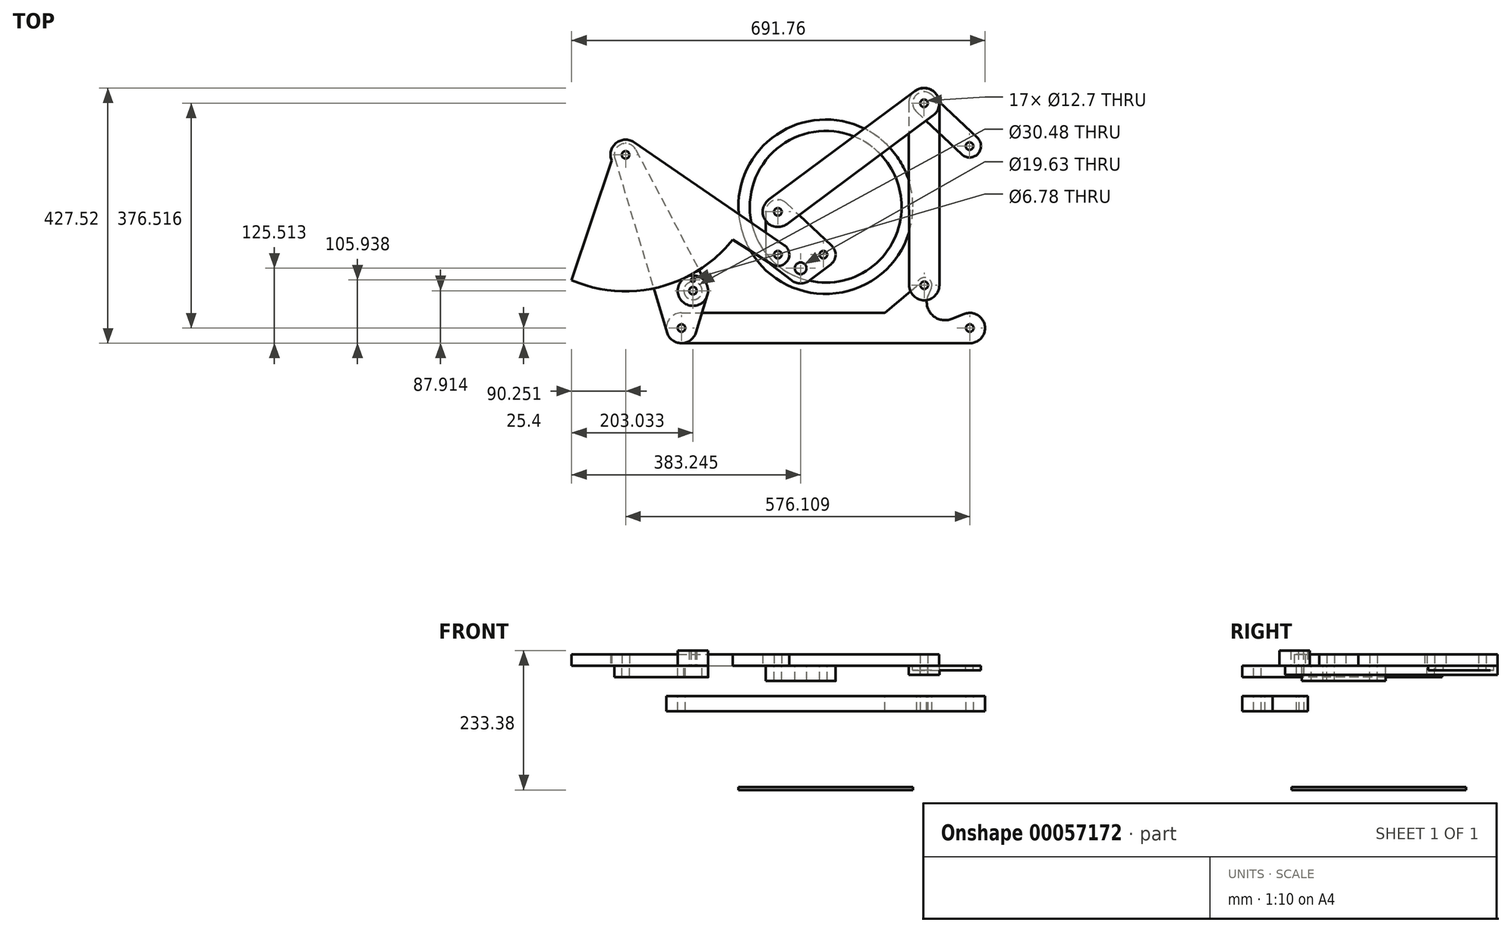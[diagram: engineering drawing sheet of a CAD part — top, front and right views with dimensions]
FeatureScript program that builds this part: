
annotation { "Feature Type Name" : "Feature", "Feature Type Description" : "" }
export const myFeature = defineFeature(function(context is Context, id is Id, definition is map)
    precondition{}
    {
        {
            var Q0;
            Q0=qCreatedBy(makeId("Top.planeOp"),FACE);
            var sketch = newSketch(context, id + "F0", { "sketchPlane" : qUnion([Q0])});
            skLineSegment(sketch, "E0.rect.bottom", {"start": v(-381, 228.6) * mm, "end": v(381, 228.6) * mm});
            skLineSegment(sketch, "E0.rect.top", {"start": v(-381, -228.6) * mm, "end": v(381, -228.6) * mm});
            skLineSegment(sketch, "E0.rect.left", {"start": v(-381, 228.6) * mm, "end": v(-381, -228.6) * mm});
            skLineSegment(sketch, "E0.rect.right", {"start": v(381, 228.6) * mm, "end": v(381, -228.6) * mm});
            skPoint(sketch, "E0.rect.middle", {"position": v(0, 0) * mm});
            skLineSegment(sketch, "E1", {"start": v(-241.3, -203.2) * mm, "end": v(241.3, -203.2) * mm, "construction": true});
            skLineSegment(sketch, "E2", {"start": v(0, -203.2) * mm, "end": v(0, 0) * mm, "construction": true});
            skLineSegment(sketch, "E3", {"start": v(-241.3, -203.2) * mm, "end": v(-334.8, 86.9) * mm});
            skLineSegment(sketch, "E4", {"start": v(-334.8, 86.9) * mm, "end": v(-79.92, -80.23) * mm});
            skLineSegment(sketch, "E5", {"start": v(-3.72, -80.23) * mm, "end": v(240.91, 101.6) * mm});
            skLineSegment(sketch, "E6", {"start": v(240.91, 101.6) * mm, "end": v(241.3, -203.2) * mm});
            skCircle(sketch, "E7", {"center": v(0, 0) * mm, "radius": 139.7 * mm});
            skArc(sketch, "E8", {"start": v(57.44, -34.77) * mm, "mid": v(188.02, -120.8) * mm, "end": v(343.35, -102.76) * mm});
            skArc(sketch, "E9", {"start": v(-425.06, -123.13) * mm, "mid": v(-268.94, -132) * mm, "end": v(-143.64, -38.45) * mm});
            skLineSegment(sketch, "E10", {"start": v(-425.06, -123.13) * mm, "end": v(-334.8, 86.9) * mm});
            skLineSegment(sketch, "E11", {"start": v(240.91, 101.6) * mm, "end": v(343.35, -102.76) * mm});
            skCircle(sketch, "E12", {"center": v(195.05, -148.23) * mm, "radius": 25.4 * mm});
            skLineSegment(sketch, "E13", {"start": v(195.05, -148.23) * mm, "end": v(241.3, -203.2) * mm});
            skCircle(sketch, "E14", {"center": v(-222.03, -140.69) * mm, "radius": 25.4 * mm});
            skLineSegment(sketch, "E15", {"start": v(-222.03, -140.69) * mm, "end": v(-241.3, -203.2) * mm});
            skLineSegment(sketch, "E16", {"start": v(-381, 76.2) * mm, "end": v(-228.6, 228.6) * mm});
            skLineSegment(sketch, "E17", {"start": v(381, 76.2) * mm, "end": v(228.6, 228.6) * mm});
            skLineSegment(sketch, "E18", {"start": v(195.05, -148.23) * mm, "end": v(240.91, 101.6) * mm, "construction": true});
            skLineSegment(sketch, "E19", {"start": v(-222.03, -140.69) * mm, "end": v(-334.8, 86.9) * mm, "construction": true});
            skLineSegment(sketch, "E20", {"start": v(-3.72, -80.23) * mm, "end": v(-79.92, -80.23) * mm});
            skLineSegment(sketch, "E21", {"start": v(-79.92, -80.23) * mm, "end": v(-79.92, -8.51) * mm});
            skLineSegment(sketch, "E22", {"start": v(-79.92, -8.51) * mm, "end": v(164.71, 173.32) * mm});
            skLineSegment(sketch, "E23", {"start": v(164.71, 173.32) * mm, "end": v(165.1, -131.48) * mm});
            skLineSegment(sketch, "E24", {"start": v(-79.92, -8.51) * mm, "end": v(-3.72, -80.23) * mm});
            skLineSegment(sketch, "E25", {"start": v(164.71, 173.32) * mm, "end": v(240.91, 101.6) * mm});
            skLineSegment(sketch, "E26", {"start": v(-41.82, -80.23) * mm, "end": v(-41.82, -103.09) * mm});
            skLineSegment(sketch, "E27", {"start": v(165.1, -131.48) * mm, "end": v(241.3, -203.2) * mm});
            skSolve(sketch);
        }
        {
            var Q0;
            Q0=qCreatedBy(makeId("Top.planeOp"),FACE);
            var sketch = newSketch(context, id + "F1", { "sketchPlane" : qUnion([Q0])});
            skCircle(sketch, "E28", {"center": v(-334.8, 86.9) * mm, "radius": 25.4 * mm});
            skCircle(sketch, "E29", {"center": v(-79.92, -80.23) * mm, "radius": 19.05 * mm});
            skArc(sketch, "E30", {"start": v(-425.06, -123.13) * mm, "mid": v(-259.1, -128.8) * mm, "end": v(-133.1, -20.65) * mm});
            skLineSegment(sketch, "E31", {"start": v(-320.44, 107.85) * mm, "end": v(-69.14, -64.52) * mm});
            skLineSegment(sketch, "E32", {"start": v(-348.3, 65.38) * mm, "end": v(-90.03, -96.37) * mm});
            skLineSegment(sketch, "E33", {"start": v(-425.06, -123.13) * mm, "end": v(-358.3, 77.22) * mm});
            skCircle(sketch, "E34", {"center": v(-334.8, 86.9) * mm, "radius": 6.35 * mm});
            skCircle(sketch, "E35", {"center": v(-79.92, -80.23) * mm, "radius": 6.35 * mm});
            skSolve(sketch);
        }
        {
            var Q0;
            Q0=makeQuery(id+"F1.imprint","IMPRINT",FACE,{"disambiguationData":[TD([[makeQuery(id+"F1.imprint","IMPRINT",EDGE,{"derivedFrom":sQuery(id+"F1.wireOp",EDGE,"E34")}),-1.0]])]});
            var Q1;
            {var subQ3=sQuery(id+"F1.wireOp",EDGE,"E28");var subQ5=sQuery(id+"F1.wireOp",EDGE,"E31");var subQ6=makeQuery(id+"F1.imprint","INTERSECT",VERTEX,{"derivedFrom":[subQ3,subQ5]});Q1=makeQuery(id+"F1.imprint","IMPRINT",FACE,{"disambiguationData":[TD([[makeQuery(id+"F1.imprint","IMPRINT",EDGE,{"disambiguationData":[TD([[subQ6,1.0]])],"derivedFrom":subQ3}),-1.0]])]});}
            var Q2;
            {var subQ3=sQuery(id+"F1.wireOp",EDGE,"E29");var subQ5=sQuery(id+"F1.wireOp",EDGE,"E31");var subQ6=makeQuery(id+"F1.imprint","INTERSECT",VERTEX,{"derivedFrom":[subQ3,subQ5]});Q2=makeQuery(id+"F1.imprint","IMPRINT",FACE,{"disambiguationData":[TD([[makeQuery(id+"F1.imprint","IMPRINT",EDGE,{"disambiguationData":[TD([[subQ6,-1.0]])],"derivedFrom":subQ3}),-1.0]])]});}
            var Q3;
            Q3=makeQuery(id+"F1.imprint","IMPRINT",FACE,{"disambiguationData":[TD([[makeQuery(id+"F1.imprint","IMPRINT",EDGE,{"derivedFrom":sQuery(id+"F1.wireOp",EDGE,"E35")}),-1.0]])]});
            var Q4;
            {var subQ0=sQuery(id+"F1.wireOp",EDGE,"E33");Q4=makeQuery(id+"F1.imprint","IMPRINT",FACE,{"disambiguationData":[TD([[makeQuery(id+"F1.imprint","IMPRINT",EDGE,{"derivedFrom":subQ0}),-1.0]])]});}
            extrude(context, id + "F2", {"entities" : qUnion([Q0, Q1, Q2, Q3, Q4]), "depth" : 19.05 * mm});
        }
        {
            var Q0;
            Q0=qCreatedBy(makeId("Top.planeOp"),FACE);
            var sketch = newSketch(context, id + "F3", { "sketchPlane" : qUnion([Q0])});
            skCircle(sketch, "E36", {"center": v(-334.8, 86.9) * mm, "radius": 19.05 * mm});
            skCircle(sketch, "E37", {"center": v(-222.03, -140.69) * mm, "radius": 25.4 * mm});
            skCircle(sketch, "E38", {"center": v(-241.3, -203.2) * mm, "radius": 25.4 * mm});
            skLineSegment(sketch, "E39", {"start": v(-353.06, 81.44) * mm, "end": v(-265.63, -210.49) * mm});
            skLineSegment(sketch, "E40", {"start": v(-317.96, 95.78) * mm, "end": v(-199.56, -128.84) * mm});
            skLineSegment(sketch, "E41", {"start": v(-217.03, -210.68) * mm, "end": v(-197.75, -148.17) * mm});
            skCircle(sketch, "E42", {"center": v(-334.8, 86.9) * mm, "radius": 6.35 * mm});
            skCircle(sketch, "E43", {"center": v(-222.03, -140.69) * mm, "radius": 15.24 * mm});
            skCircle(sketch, "E44", {"center": v(-241.3, -203.2) * mm, "radius": 6.35 * mm});
            skSolve(sketch);
        }
        {
            var Q0;
            Q0=makeQuery(id+"F3.imprint","IMPRINT",FACE,{"disambiguationData":[TD([[makeQuery(id+"F3.imprint","IMPRINT",EDGE,{"derivedFrom":sQuery(id+"F3.wireOp",EDGE,"E42")}),-1.0]])]});
            var Q1;
            {var subQ2=sQuery(id+"F3.wireOp",EDGE,"E39");Q1=makeQuery(id+"F3.imprint","IMPRINT",FACE,{"disambiguationData":[TD([[makeQuery(id+"F3.imprint","IMPRINT",EDGE,{"derivedFrom":subQ2}),1.0]])]});}
            var Q2;
            Q2=makeQuery(id+"F3.imprint","IMPRINT",FACE,{"disambiguationData":[TD([[makeQuery(id+"F3.imprint","IMPRINT",EDGE,{"derivedFrom":sQuery(id+"F3.wireOp",EDGE,"E43")}),-1.0]])]});
            var Q3;
            Q3=makeQuery(id+"F3.imprint","IMPRINT",FACE,{"disambiguationData":[TD([[makeQuery(id+"F3.imprint","IMPRINT",EDGE,{"derivedFrom":sQuery(id+"F3.wireOp",EDGE,"E44")}),-1.0]])]});
            extrude(context, id + "F4", {"entities" : qUnion([Q0, Q1, Q2, Q3]), "oppositeDirection" : true, "depth" : 19.05 * mm});
        }
        {
            var Q0;
            Q0=qCreatedBy(makeId("Top.planeOp"),FACE);
            var sketch = newSketch(context, id + "F5", { "sketchPlane" : qUnion([Q0])});
            skCircle(sketch, "E45", {"center": v(-222.03, -140.69) * mm, "radius": 25.4 * mm});
            skCircle(sketch, "E46", {"center": v(-222.03, -140.69) * mm, "radius": 6.35 * mm});
            skCircle(sketch, "E47", {"center": v(-222.03, -122.66) * mm, "radius": 3.4 * mm});
            skSolve(sketch);
        }
        {
            var Q0;
            Q0=makeQuery(id+"F5.imprint","IMPRINT",FACE,{"disambiguationData":[TD([[makeQuery(id+"F5.imprint","IMPRINT",EDGE,{"derivedFrom":sQuery(id+"F5.wireOp",EDGE,"E45")}),1.0]])]});
            extrude(context, id + "F6", {"entities" : qUnion([Q0]), "depth" : 25.4 * mm});
        }
        {
            var Q0;
            Q0=qCreatedBy(makeId("Top.planeOp"),FACE);
            var sketch = newSketch(context, id + "F7", { "sketchPlane" : qUnion([Q0])});
            skCircle(sketch, "E48", {"center": v(-79.92, -8.51) * mm, "radius": 20.32 * mm});
            skCircle(sketch, "E49", {"center": v(-79.92, -80.23) * mm, "radius": 20.32 * mm});
            skCircle(sketch, "E50", {"center": v(-3.72, -80.23) * mm, "radius": 20.32 * mm});
            skLineSegment(sketch, "E51", {"start": v(-65.99, 6.29) * mm, "end": v(10.21, -65.43) * mm});
            skLineSegment(sketch, "E52", {"start": v(-100.24, -8.51) * mm, "end": v(-100.24, -80.23) * mm});
            skCircle(sketch, "E53", {"center": v(-79.92, -8.51) * mm, "radius": 6.35 * mm});
            skCircle(sketch, "E54", {"center": v(-79.92, -80.23) * mm, "radius": 6.35 * mm});
            skCircle(sketch, "E55", {"center": v(-3.72, -80.23) * mm, "radius": 6.35 * mm});
            skCircle(sketch, "E56", {"center": v(-41.82, -103.09) * mm, "radius": 25.4 * mm});
            skLineSegment(sketch, "E57", {"start": v(-92.3, -96.34) * mm, "end": v(-57.29, -123.23) * mm});
            skLineSegment(sketch, "E58", {"start": v(8.66, -96.34) * mm, "end": v(-26.34, -123.23) * mm});
            skCircle(sketch, "E59", {"center": v(-41.82, -103.09) * mm, "radius": 9.81 * mm});
            skSolve(sketch);
        }
        {
            var Q0;
            Q0=makeQuery(id+"F7.imprint","IMPRINT",FACE,{"disambiguationData":[TD([[makeQuery(id+"F7.imprint","IMPRINT",EDGE,{"derivedFrom":sQuery(id+"F7.wireOp",EDGE,"E53")}),-1.0]])]});
            var Q1;
            {var subQ5=sQuery(id+"F7.wireOp",EDGE,"E51");Q1=makeQuery(id+"F7.imprint","IMPRINT",FACE,{"disambiguationData":[TD([[makeQuery(id+"F7.imprint","IMPRINT",EDGE,{"derivedFrom":subQ5}),-1.0]])]});}
            var Q2;
            {var subQ0=sQuery(id+"F7.wireOp",EDGE,"E57");Q2=makeQuery(id+"F7.imprint","IMPRINT",FACE,{"disambiguationData":[TD([[makeQuery(id+"F7.imprint","IMPRINT",EDGE,{"derivedFrom":subQ0}),1.0]])]});}
            var Q3;
            Q3=makeQuery(id+"F7.imprint","IMPRINT",FACE,{"disambiguationData":[TD([[makeQuery(id+"F7.imprint","IMPRINT",EDGE,{"derivedFrom":sQuery(id+"F7.wireOp",EDGE,"E54")}),-1.0]])]});
            var Q4;
            Q4=makeQuery(id+"F7.imprint","IMPRINT",FACE,{"disambiguationData":[TD([[makeQuery(id+"F7.imprint","IMPRINT",EDGE,{"derivedFrom":sQuery(id+"F7.wireOp",EDGE,"E59")}),-1.0]])]});
            var Q5;
            {var subQ0=sQuery(id+"F7.wireOp",EDGE,"E56");var subQ1=sQuery(id+"F7.wireOp",EDGE,"E49");var subQ3=makeQuery(id+"F7.imprint","INTERSECT",VERTEX,{"disambiguationData":[OD(0.0)],"derivedFrom":[subQ1,subQ0]});Q5=makeQuery(id+"F7.imprint","IMPRINT",FACE,{"disambiguationData":[TD([[makeQuery(id+"F7.imprint","IMPRINT",EDGE,{"disambiguationData":[TD([[subQ3,-1.0]])],"derivedFrom":subQ1}),1.0]])]});}
            var Q6;
            {var subQ0=sQuery(id+"F7.wireOp",EDGE,"E56");var subQ1=sQuery(id+"F7.wireOp",EDGE,"E50");var subQ3=makeQuery(id+"F7.imprint","INTERSECT",VERTEX,{"disambiguationData":[OD(0.0)],"derivedFrom":[subQ1,subQ0]});Q6=makeQuery(id+"F7.imprint","IMPRINT",FACE,{"disambiguationData":[TD([[makeQuery(id+"F7.imprint","IMPRINT",EDGE,{"disambiguationData":[TD([[subQ3,-1.0]])],"derivedFrom":subQ1}),1.0]])]});}
            var Q7;
            Q7=makeQuery(id+"F7.imprint","IMPRINT",FACE,{"disambiguationData":[TD([[makeQuery(id+"F7.imprint","IMPRINT",EDGE,{"derivedFrom":sQuery(id+"F7.wireOp",EDGE,"E55")}),-1.0]])]});
            var Q8;
            {var subQ0=sQuery(id+"F7.wireOp",EDGE,"E58");Q8=makeQuery(id+"F7.imprint","IMPRINT",FACE,{"disambiguationData":[TD([[makeQuery(id+"F7.imprint","IMPRINT",EDGE,{"derivedFrom":subQ0}),-1.0]])]});}
            extrude(context, id + "F8", {"entities" : qUnion([Q0, Q1, Q2, Q3, Q4, Q5, Q6, Q7, Q8]), "oppositeDirection" : true, "depth" : 25.4 * mm});
        }
        {
            var Q0;
            Q0=qCreatedBy(makeId("Top.planeOp"),FACE);
            cPlane(context, id + "F9", {"entities" : qUnion([Q0]), "cplaneType" : CPlaneType.OFFSET, "offset" : 50.8 * mm, "oppositeDirection" : true, "width" : 152.4 * mm, "height" : 152.4 * mm});
        }
        {
            var Q0;
            Q0=qCreatedBy(id+"F9.planeOp",FACE);
            var sketch = newSketch(context, id + "F10", { "sketchPlane" : qUnion([Q0])});
            skCircle(sketch, "E60", {"center": v(-241.3, -203.2) * mm, "radius": 25.4 * mm});
            skCircle(sketch, "E61", {"center": v(241.3, -203.2) * mm, "radius": 25.4 * mm});
            skCircle(sketch, "E62", {"center": v(165.1, -131.48) * mm, "radius": 12.7 * mm});
            skLineSegment(sketch, "E63", {"start": v(-241.3, -228.6) * mm, "end": v(241.3, -228.6) * mm});
            skLineSegment(sketch, "E64", {"start": v(-241.3, -177.8) * mm, "end": v(99.01, -177.8) * mm});
            skLineSegment(sketch, "E65", {"start": v(99.01, -177.8) * mm, "end": v(152.48, -132.93) * mm});
            skCircle(sketch, "E66", {"center": v(-241.3, -203.2) * mm, "radius": 6.35 * mm});
            skCircle(sketch, "E67", {"center": v(241.3, -203.2) * mm, "radius": 6.35 * mm});
            skCircle(sketch, "E68", {"center": v(165.1, -131.48) * mm, "radius": 6.35 * mm});
            skLineSegment(sketch, "E69", {"start": v(211, -187.94) * mm, "end": v(231.89, -179.6) * mm});
            skLineSegment(sketch, "E70", {"start": v(176.65, -136.76) * mm, "end": v(172, -146.96) * mm});
            skPoint(sketch, "E71.visualSharp", {"position": v(140.4, -216.11) * mm});
            skArc(sketch, "E71.filletArc", {"start": v(172, -146.96) * mm, "mid": v(177.64, -180.65) * mm, "end": v(211, -187.94) * mm});
            skSolve(sketch);
        }
        {
            var Q0;
            Q0=makeQuery(id+"F10.imprint","IMPRINT",FACE,{"disambiguationData":[TD([[makeQuery(id+"F10.imprint","IMPRINT",EDGE,{"derivedFrom":sQuery(id+"F10.wireOp",EDGE,"E66")}),-1.0]])]});
            var Q1;
            {var subQ3=sQuery(id+"F10.wireOp",EDGE,"E63");Q1=makeQuery(id+"F10.imprint","IMPRINT",FACE,{"disambiguationData":[TD([[makeQuery(id+"F10.imprint","IMPRINT",EDGE,{"derivedFrom":subQ3}),1.0]])]});}
            var Q2;
            Q2=makeQuery(id+"F10.imprint","IMPRINT",FACE,{"disambiguationData":[TD([[makeQuery(id+"F10.imprint","IMPRINT",EDGE,{"derivedFrom":sQuery(id+"F10.wireOp",EDGE,"E68")}),-1.0]])]});
            var Q3;
            Q3=makeQuery(id+"F10.imprint","IMPRINT",FACE,{"disambiguationData":[TD([[makeQuery(id+"F10.imprint","IMPRINT",EDGE,{"derivedFrom":sQuery(id+"F10.wireOp",EDGE,"E67")}),-1.0]])]});
            extrude(context, id + "F11", {"entities" : qUnion([Q0, Q1, Q2, Q3]), "oppositeDirection" : true, "depth" : 25.4 * mm});
        }
        {
            var Q0;
            Q0=qCreatedBy(makeId("Top.planeOp"),FACE);
            var sketch = newSketch(context, id + "F12", { "sketchPlane" : qUnion([Q0])});
            skCircle(sketch, "E72", {"center": v(-79.92, -8.51) * mm, "radius": 25.4 * mm});
            skCircle(sketch, "E73", {"center": v(164.71, 173.32) * mm, "radius": 25.4 * mm});
            skLineSegment(sketch, "E74", {"start": v(149.56, 193.7) * mm, "end": v(-95.07, 11.87) * mm});
            skLineSegment(sketch, "E75", {"start": v(179.86, 152.93) * mm, "end": v(-64.76, -28.9) * mm});
            skCircle(sketch, "E76", {"center": v(-79.92, -8.51) * mm, "radius": 6.35 * mm});
            skCircle(sketch, "E77", {"center": v(164.71, 173.32) * mm, "radius": 6.35 * mm});
            skSolve(sketch);
        }
        {
            var Q0;
            Q0=makeQuery(id+"F12.imprint","IMPRINT",FACE,{"disambiguationData":[TD([[makeQuery(id+"F12.imprint","IMPRINT",EDGE,{"derivedFrom":sQuery(id+"F12.wireOp",EDGE,"E76")}),-1.0]])]});
            var Q1;
            {var subQ1=sQuery(id+"F12.wireOp",EDGE,"E74");Q1=makeQuery(id+"F12.imprint","IMPRINT",FACE,{"disambiguationData":[TD([[makeQuery(id+"F12.imprint","IMPRINT",EDGE,{"derivedFrom":subQ1}),1.0]])]});}
            var Q2;
            Q2=makeQuery(id+"F12.imprint","IMPRINT",FACE,{"disambiguationData":[TD([[makeQuery(id+"F12.imprint","IMPRINT",EDGE,{"derivedFrom":sQuery(id+"F12.wireOp",EDGE,"E77")}),-1.0]])]});
            extrude(context, id + "F13", {"entities" : qUnion([Q0, Q1, Q2]), "depth" : 19.05 * mm});
        }
        {
            var Q0;
            Q0=qCreatedBy(makeId("Top.planeOp"),FACE);
            var sketch = newSketch(context, id + "F14", { "sketchPlane" : qUnion([Q0])});
            skCircle(sketch, "E78", {"center": v(164.71, 173.32) * mm, "radius": 25.6 * mm});
            skCircle(sketch, "E79", {"center": v(165.1, -131.48) * mm, "radius": 25.17 * mm});
            skLineSegment(sketch, "E80", {"start": v(139.1, 173.25) * mm, "end": v(139.93, -131.55) * mm});
            skLineSegment(sketch, "E81", {"start": v(190.32, 173.31) * mm, "end": v(190.27, -131.49) * mm});
            skCircle(sketch, "E82", {"center": v(164.71, 173.32) * mm, "radius": 6.35 * mm});
            skCircle(sketch, "E83", {"center": v(165.1, -131.48) * mm, "radius": 6.35 * mm});
            skSolve(sketch);
        }
        {
            var Q0;
            Q0=makeQuery(id+"F14.imprint","IMPRINT",FACE,{"disambiguationData":[TD([[makeQuery(id+"F14.imprint","IMPRINT",EDGE,{"derivedFrom":sQuery(id+"F14.wireOp",EDGE,"E82")}),-1.0]])]});
            var Q1;
            {var subQ1=sQuery(id+"F14.wireOp",EDGE,"E80");Q1=makeQuery(id+"F14.imprint","IMPRINT",FACE,{"disambiguationData":[TD([[makeQuery(id+"F14.imprint","IMPRINT",EDGE,{"derivedFrom":subQ1}),1.0]])]});}
            var Q2;
            Q2=makeQuery(id+"F14.imprint","IMPRINT",FACE,{"disambiguationData":[TD([[makeQuery(id+"F14.imprint","IMPRINT",EDGE,{"derivedFrom":sQuery(id+"F14.wireOp",EDGE,"E83")}),-1.0]])]});
            extrude(context, id + "F15", {"entities" : qUnion([Q0, Q1, Q2]), "oppositeDirection" : true, "depth" : 15.24 * mm});
        }
        {
            var Q0;
            Q0=qCreatedBy(makeId("Top.planeOp"),FACE);
            var sketch = newSketch(context, id + "F16", { "sketchPlane" : qUnion([Q0])});
            skCircle(sketch, "E84", {"center": v(164.71, 173.32) * mm, "radius": 19.05 * mm});
            skCircle(sketch, "E85", {"center": v(240.91, 101.6) * mm, "radius": 19.05 * mm});
            skLineSegment(sketch, "E86", {"start": v(177.77, 187.19) * mm, "end": v(253.97, 115.47) * mm});
            skLineSegment(sketch, "E87", {"start": v(151.65, 159.44) * mm, "end": v(227.85, 87.73) * mm});
            skCircle(sketch, "E88", {"center": v(240.91, 101.6) * mm, "radius": 6.35 * mm});
            skCircle(sketch, "E89", {"center": v(164.71, 173.32) * mm, "radius": 6.35 * mm});
            skSolve(sketch);
        }
        {
            var Q0;
            Q0=makeQuery(id+"F16.imprint","IMPRINT",FACE,{"disambiguationData":[TD([[makeQuery(id+"F16.imprint","IMPRINT",EDGE,{"derivedFrom":sQuery(id+"F16.wireOp",EDGE,"E89")}),-1.0]])]});
            var Q1;
            {var subQ1=sQuery(id+"F16.wireOp",EDGE,"E86");Q1=makeQuery(id+"F16.imprint","IMPRINT",FACE,{"disambiguationData":[TD([[makeQuery(id+"F16.imprint","IMPRINT",EDGE,{"derivedFrom":subQ1}),-1.0]])]});}
            var Q2;
            Q2=makeQuery(id+"F16.imprint","IMPRINT",FACE,{"disambiguationData":[TD([[makeQuery(id+"F16.imprint","IMPRINT",EDGE,{"derivedFrom":sQuery(id+"F16.wireOp",EDGE,"E88")}),-1.0]])]});
            extrude(context, id + "F17", {"entities" : qUnion([Q0, Q1, Q2]), "oppositeDirection" : true, "depth" : 7.62 * mm});
        }
        {
            var Q0;
            Q0=qCreatedBy(makeId("Top.planeOp"),FACE);
            cPlane(context, id + "F18", {"entities" : qUnion([Q0]), "cplaneType" : CPlaneType.OFFSET, "offset" : 203.2 * mm, "oppositeDirection" : true, "width" : 152.4 * mm, "height" : 152.4 * mm});
        }
        {
            var Q0;
            Q0=qCreatedBy(id+"F18.planeOp",FACE);
            var sketch = newSketch(context, id + "F19", { "sketchPlane" : qUnion([Q0])});
            skCircle(sketch, "E90", {"center": v(0, 0) * mm, "radius": 146.05 * mm});
            skCircle(sketch, "E91", {"center": v(0, 0) * mm, "radius": 127 * mm});
            skSolve(sketch);
        }
        {
            var Q0;
            Q0=makeQuery(id+"F19.imprint","IMPRINT",FACE,{"disambiguationData":[TD([[makeQuery(id+"F19.imprint","IMPRINT",EDGE,{"derivedFrom":sQuery(id+"F19.wireOp",EDGE,"E90")}),1.0]])]});
            var Q1;
            Q1=makeQuery(id+"F19.imprint","IMPRINT",FACE,{"disambiguationData":[TD([[makeQuery(id+"F19.imprint","IMPRINT",EDGE,{"derivedFrom":sQuery(id+"F19.wireOp",EDGE,"E91")}),1.0]])]});
            extrude(context, id + "F20", {"entities" : qUnion([Q0, Q1]), "oppositeDirection" : true, "depth" : 4.78 * mm});
        }
        {
            var Q0;
            Q0=makeQuery(id+"F19.imprint","IMPRINT",FACE,{"disambiguationData":[TD([[makeQuery(id+"F19.imprint","IMPRINT",EDGE,{"derivedFrom":sQuery(id+"F19.wireOp",EDGE,"E91")}),1.0]])]});
            extrude(context, id + "F21", {"entities" : qUnion([Q0]), "operationType" : NewBodyOperationType.ADD, "depth" : 0.25 * mm});
        }
    });
